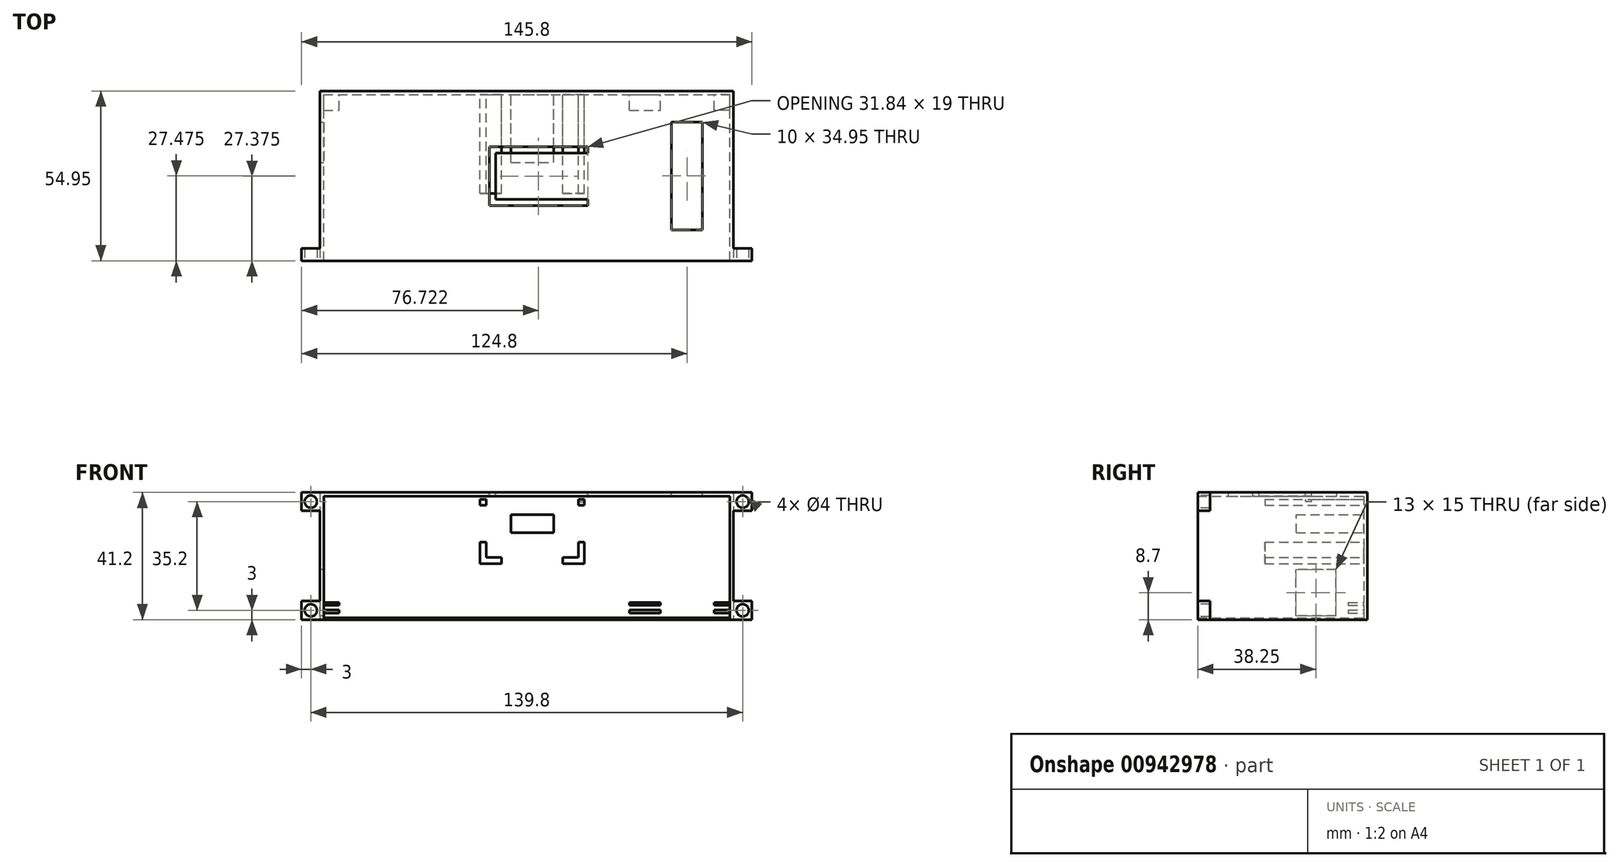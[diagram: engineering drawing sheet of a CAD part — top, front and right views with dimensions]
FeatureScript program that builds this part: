
annotation { "Feature Type Name" : "Feature", "Feature Type Description" : "" }
export const myFeature = defineFeature(function(context is Context, id is Id, definition is map)
    precondition{}
    {
        {
            var Q0;
            Q0=qCreatedBy(makeId("Top.planeOp"),FACE);
            var sketch = newSketch(context, id + "F0", { "sketchPlane" : qUnion([Q0])});
            skLineSegment(sketch, "E0.top", {"start": v(0, 53.75) * mm, "end": v(131.4, 53.75) * mm});
            skLineSegment(sketch, "E0.left", {"start": v(0, 0) * mm, "end": v(0, 53.75) * mm});
            skLineSegment(sketch, "E0.right", {"start": v(131.4, 0) * mm, "end": v(131.4, 53.75) * mm});
            skLineSegment(sketch, "E1.bottom", {"start": v(0, 0) * mm, "end": v(-1.2, 0) * mm});
            skLineSegment(sketch, "E1.top", {"start": v(0, 54.95) * mm, "end": v(-1.2, 54.95) * mm});
            skLineSegment(sketch, "E1.right", {"start": v(-1.2, 0) * mm, "end": v(-1.2, 54.95) * mm});
            skLineSegment(sketch, "E2.bottom", {"start": v(0, 54.95) * mm, "end": v(132.6, 54.95) * mm});
            skLineSegment(sketch, "E2.right", {"start": v(132.6, 54.95) * mm, "end": v(132.6, 53.75) * mm});
            skLineSegment(sketch, "E3.top", {"start": v(132.6, 0) * mm, "end": v(131.4, 0) * mm});
            skLineSegment(sketch, "E3.left", {"start": v(132.6, 53.75) * mm, "end": v(132.6, 0) * mm});
            skSolve(sketch);
        }
        {
            var Q0;
            Q0 = qSketchRegion(id + "F0", true);
            extrude(context, id + "F1", {"entities" : qUnion([Q0]), "depth" : 40 * mm, "offsetDistance" : 25 * mm});
        }
        {
            var Q0;
            Q0=makeQuery(id+"F1.opExtrude","CAP_FACE",FACE,{"disambiguationData":[OSD([sQuery(id+"F0.wireOp",EDGE,"E0.top"),sQuery(id+"F0.wireOp",EDGE,"E0.left"),sQuery(id+"F0.wireOp",EDGE,"E0.right"),sQuery(id+"F0.wireOp",EDGE,"E1.bottom"),sQuery(id+"F0.wireOp",EDGE,"E1.top"),sQuery(id+"F0.wireOp",EDGE,"E1.right"),sQuery(id+"F0.wireOp",EDGE,"E2.bottom"),sQuery(id+"F0.wireOp",EDGE,"E2.right"),sQuery(id+"F0.wireOp",EDGE,"E3.top"),sQuery(id+"F0.wireOp",EDGE,"E3.left")])],"isStart":true});
            var sketch = newSketch(context, id + "F2", { "sketchPlane" : qUnion([Q0])});
            skLineSegment(sketch, "E4.bottom", {"start": v(0, 0) * mm, "end": v(131.4, 0) * mm});
            skLineSegment(sketch, "E4.top", {"start": v(0, -53.75) * mm, "end": v(131.4, -53.75) * mm});
            skLineSegment(sketch, "E4.left", {"start": v(0, 0) * mm, "end": v(0, -53.75) * mm});
            skLineSegment(sketch, "E4.right", {"start": v(131.4, 0) * mm, "end": v(131.4, -53.75) * mm});
            skSolve(sketch);
        }
        {
            var Q0;
            Q0 = qSketchRegion(id + "F2", true);
            extrude(context, id + "F3", {"entities" : qUnion([Q0]), "oppositeDirection" : true, "depth" : 0.6 * mm, "offsetDistance" : 25 * mm});
        }
        {
            var Q0;
            Q0=makeQuery(id+"F1.opExtrude","SWEPT_FACE",FACE,{"disambiguationData":[OSD([sQuery(id+"F0.wireOp",EDGE,"E0.top")])]});
            var sketch = newSketch(context, id + "F4", { "sketchPlane" : qUnion([Q0])});
            skLineSegment(sketch, "E5.bottom", {"start": v(0, 2.1) * mm, "end": v(5, 2.1) * mm});
            skLineSegment(sketch, "E5.top", {"start": v(0, 3.1) * mm, "end": v(5, 3.1) * mm});
            skLineSegment(sketch, "E5.left", {"start": v(0, 2.1) * mm, "end": v(0, 3.1) * mm});
            skLineSegment(sketch, "E5.right", {"start": v(5, 2.1) * mm, "end": v(5, 3.1) * mm});
            skLineSegment(sketch, "E6.bottom", {"start": v(0, 4.6) * mm, "end": v(5, 4.6) * mm});
            skLineSegment(sketch, "E6.top", {"start": v(0, 5.6) * mm, "end": v(5, 5.6) * mm});
            skLineSegment(sketch, "E6.left", {"start": v(0, 4.6) * mm, "end": v(0, 5.6) * mm});
            skLineSegment(sketch, "E6.right", {"start": v(5, 4.6) * mm, "end": v(5, 5.6) * mm});
            skLineSegment(sketch, "E7.bottom", {"start": v(131.4, 2.1) * mm, "end": v(126.4, 2.1) * mm});
            skLineSegment(sketch, "E7.top", {"start": v(131.4, 3.1) * mm, "end": v(126.4, 3.1) * mm});
            skLineSegment(sketch, "E7.left", {"start": v(131.4, 2.1) * mm, "end": v(131.4, 3.1) * mm});
            skLineSegment(sketch, "E7.right", {"start": v(126.4, 2.1) * mm, "end": v(126.4, 3.1) * mm});
            skLineSegment(sketch, "E8.bottom", {"start": v(131.4, 4.6) * mm, "end": v(126.4, 4.6) * mm});
            skLineSegment(sketch, "E8.top", {"start": v(131.4, 5.6) * mm, "end": v(126.4, 5.6) * mm});
            skLineSegment(sketch, "E8.left", {"start": v(131.4, 4.6) * mm, "end": v(131.4, 5.6) * mm});
            skLineSegment(sketch, "E8.right", {"start": v(126.4, 4.6) * mm, "end": v(126.4, 5.6) * mm});
            skLineSegment(sketch, "E9.bottom", {"start": v(99, 3.1) * mm, "end": v(109, 3.1) * mm});
            skLineSegment(sketch, "E9.top", {"start": v(99, 2.1) * mm, "end": v(109, 2.1) * mm});
            skLineSegment(sketch, "E9.left", {"start": v(99, 3.1) * mm, "end": v(99, 2.1) * mm});
            skLineSegment(sketch, "E9.right", {"start": v(109, 3.1) * mm, "end": v(109, 2.1) * mm});
            skLineSegment(sketch, "E10.bottom", {"start": v(99, 4.6) * mm, "end": v(109, 4.6) * mm});
            skLineSegment(sketch, "E10.top", {"start": v(99, 5.6) * mm, "end": v(109, 5.6) * mm});
            skLineSegment(sketch, "E10.left", {"start": v(99, 4.6) * mm, "end": v(99, 5.6) * mm});
            skLineSegment(sketch, "E10.right", {"start": v(109, 4.6) * mm, "end": v(109, 5.6) * mm});
            skSolve(sketch);
        }
        {
            var Q0;
            Q0 = qSketchRegion(id + "F4", true);
            extrude(context, id + "F5", {"entities" : qUnion([Q0]), "operationType" : NewBodyOperationType.ADD, "depth" : 5 * mm, "offsetDistance" : 25 * mm});
        }
        {
            var Q0;
            Q0=makeQuery(id+"F1.opExtrude","SWEPT_FACE",FACE,{"disambiguationData":[OSD([sQuery(id+"F0.wireOp",EDGE,"E0.top")])]});
            var sketch = newSketch(context, id + "F6", { "sketchPlane" : qUnion([Q0])});
            skLineSegment(sketch, "E11.bottom", {"start": v(52.6, 39) * mm, "end": v(82.4, 39) * mm, "construction": true});
            skLineSegment(sketch, "E11.top", {"start": v(52.6, 20.1) * mm, "end": v(82.4, 20.1) * mm, "construction": true});
            skLineSegment(sketch, "E11.left", {"start": v(52.6, 39) * mm, "end": v(52.6, 20.1) * mm, "construction": true});
            skLineSegment(sketch, "E11.right", {"start": v(82.4, 39) * mm, "end": v(82.4, 20.1) * mm, "construction": true});
            skLineSegment(sketch, "E12", {"start": v(52.6, 20.1) * mm, "end": v(57.6, 20.1) * mm});
            skLineSegment(sketch, "E13", {"start": v(57.6, 20.1) * mm, "end": v(57.6, 18.1) * mm});
            skLineSegment(sketch, "E14", {"start": v(57.6, 18.1) * mm, "end": v(50.6, 18.1) * mm});
            skLineSegment(sketch, "E15", {"start": v(50.6, 18.1) * mm, "end": v(50.6, 25.1) * mm});
            skLineSegment(sketch, "E16", {"start": v(50.6, 25.1) * mm, "end": v(52.6, 25.1) * mm});
            skLineSegment(sketch, "E17", {"start": v(52.6, 25.1) * mm, "end": v(52.6, 20.1) * mm});
            skLineSegment(sketch, "E18", {"start": v(77.4, 20.1) * mm, "end": v(82.4, 20.1) * mm});
            skLineSegment(sketch, "E19", {"start": v(82.4, 25.1) * mm, "end": v(84.4, 25.1) * mm});
            skLineSegment(sketch, "E20", {"start": v(84.4, 25.1) * mm, "end": v(84.4, 18.1) * mm});
            skLineSegment(sketch, "E21", {"start": v(84.4, 18.1) * mm, "end": v(77.4, 18.1) * mm});
            skLineSegment(sketch, "E22", {"start": v(77.4, 18.1) * mm, "end": v(77.4, 20.1) * mm});
            skLineSegment(sketch, "E23.bottom", {"start": v(82.4, 39) * mm, "end": v(84.4, 39) * mm});
            skLineSegment(sketch, "E23.top", {"start": v(82.4, 37) * mm, "end": v(84.4, 37) * mm});
            skLineSegment(sketch, "E23.left", {"start": v(82.4, 39) * mm, "end": v(82.4, 37) * mm});
            skLineSegment(sketch, "E23.right", {"start": v(84.4, 39) * mm, "end": v(84.4, 37) * mm});
            skLineSegment(sketch, "E24.bottom", {"start": v(52.6, 39) * mm, "end": v(50.6, 39) * mm});
            skLineSegment(sketch, "E24.top", {"start": v(52.6, 37) * mm, "end": v(50.6, 37) * mm});
            skLineSegment(sketch, "E24.left", {"start": v(52.6, 39) * mm, "end": v(52.6, 37) * mm});
            skLineSegment(sketch, "E24.right", {"start": v(50.6, 39) * mm, "end": v(50.6, 37) * mm});
            skLineSegment(sketch, "E25", {"start": v(82.4, 20.1) * mm, "end": v(82.4, 25.1) * mm});
            skSolve(sketch);
        }
        {
            var Q0;
            Q0 = qSketchRegion(id + "F6", true);
            var Q1;
            Q1=makeQuery(id+"F1.opExtrude","SWEPT_BODY",BODY,{"disambiguationData":[OSD([sQuery(id+"F0.wireOp",EDGE,"E0.top"),sQuery(id+"F0.wireOp",EDGE,"E0.left"),sQuery(id+"F0.wireOp",EDGE,"E0.right"),sQuery(id+"F0.wireOp",EDGE,"E1.bottom"),sQuery(id+"F0.wireOp",EDGE,"E1.top"),sQuery(id+"F0.wireOp",EDGE,"E1.right"),sQuery(id+"F0.wireOp",EDGE,"E2.bottom"),sQuery(id+"F0.wireOp",EDGE,"E2.right"),sQuery(id+"F0.wireOp",EDGE,"E3.top"),sQuery(id+"F0.wireOp",EDGE,"E3.left")])]});
            extrude(context, id + "F7", {"entities" : qUnion([Q0]), "operationType" : NewBodyOperationType.ADD, "depth" : 32 * mm, "endBoundEntityBody" : qUnion([Q1]), "offsetDistance" : 25 * mm});
        }
        {
            var Q0;
            Q0=makeQuery(id+"F1.opExtrude","SWEPT_FACE",FACE,{"disambiguationData":[OSD([sQuery(id+"F0.wireOp",EDGE,"E0.top")])]});
            var sketch = newSketch(context, id + "F8", { "sketchPlane" : qUnion([Q0])});
            skLineSegment(sketch, "E26.bottom", {"start": v(60.6, 28.1) * mm, "end": v(74.4, 28.1) * mm});
            skLineSegment(sketch, "E26.top", {"start": v(60.6, 34) * mm, "end": v(74.4, 34) * mm});
            skLineSegment(sketch, "E26.left", {"start": v(60.6, 28.1) * mm, "end": v(60.6, 34) * mm});
            skLineSegment(sketch, "E26.right", {"start": v(74.4, 28.1) * mm, "end": v(74.4, 34) * mm});
            skSolve(sketch);
        }
        {
            var Q0;
            Q0 = qSketchRegion(id + "F8", true);
            extrude(context, id + "F9", {"entities" : qUnion([Q0]), "operationType" : NewBodyOperationType.ADD, "depth" : (53.75 / 2 - 5) * mm, "offsetDistance" : 25 * mm});
        }
        {
            var Q0;
            Q0=makeQuery(id+"F1.opExtrude","SWEPT_FACE",FACE,{"disambiguationData":[OSD([sQuery(id+"F0.wireOp",EDGE,"E1.top"),sQuery(id+"F0.wireOp",EDGE,"E2.bottom")])]});
            var sketch = newSketch(context, id + "F10", { "sketchPlane" : qUnion([Q0])});
            skLineSegment(sketch, "E27.bottom", {"start": v(-131.4, 40) * mm, "end": v(-132.6, 40) * mm});
            skLineSegment(sketch, "E27.top", {"start": v(-127.4, 41.2) * mm, "end": v(-132.6, 41.2) * mm});
            skLineSegment(sketch, "E27.right", {"start": v(-132.6, 40) * mm, "end": v(-132.6, 41.2) * mm});
            skLineSegment(sketch, "E28.bottom", {"start": v(1.2, 40) * mm, "end": v(-127.4, 40) * mm});
            skLineSegment(sketch, "E28.top", {"start": v(1.2, 41.2) * mm, "end": v(-127.4, 41.2) * mm});
            skLineSegment(sketch, "E28.left", {"start": v(1.2, 40) * mm, "end": v(1.2, 41.2) * mm});
            skLineSegment(sketch, "E29", {"start": v(-127.4, 40) * mm, "end": v(-131.4, 40) * mm});
            skSolve(sketch);
        }
        {
            var Q0;
            Q0 = qSketchRegion(id + "F10", true);
            var Q1;
            Q1=makeQuery(id+"F1.opExtrude","SWEPT_FACE",FACE,{"disambiguationData":[OSD([sQuery(id+"F0.wireOp",EDGE,"E1.bottom")])]});
            extrude(context, id + "F11", {"entities" : qUnion([Q0]), "operationType" : NewBodyOperationType.ADD, "endBound" : BoundingType.UP_TO_SURFACE, "oppositeDirection" : true, "depth" : 25 * mm, "endBoundEntityFace" : qUnion([Q1]), "offsetDistance" : 25 * mm});
        }
        {
            var Q0;
            Q0=makeQuery(id+"F11.opExtrude","SWEPT_FACE",FACE,{"disambiguationData":[OSD([sQuery(id+"F10.wireOp",EDGE,"E27.top"),sQuery(id+"F10.wireOp",EDGE,"E28.top")])]});
            var sketch = newSketch(context, id + "F12", { "sketchPlane" : qUnion([Q0])});
            skLineSegment(sketch, "E30", {"start": v(85.44, 36.88) * mm, "end": v(53.6, 36.88) * mm});
            skLineSegment(sketch, "E31", {"start": v(53.6, 36.88) * mm, "end": v(53.6, 17.88) * mm});
            skLineSegment(sketch, "E32", {"start": v(53.6, 17.88) * mm, "end": v(85.44, 17.88) * mm});
            skLineSegment(sketch, "E33", {"start": v(85.44, 17.88) * mm, "end": v(85.44, 19.88) * mm});
            skLineSegment(sketch, "E34", {"start": v(85.44, 19.88) * mm, "end": v(55.6, 19.88) * mm});
            skLineSegment(sketch, "E35", {"start": v(55.6, 19.87) * mm, "end": v(55.6, 34.87) * mm});
            skLineSegment(sketch, "E36", {"start": v(55.6, 34.87) * mm, "end": v(85.44, 34.87) * mm});
            skLineSegment(sketch, "E37", {"start": v(85.44, 34.87) * mm, "end": v(85.44, 36.88) * mm});
            skLineSegment(sketch, "E38.bottom", {"start": v(122.6, 10) * mm, "end": v(112.6, 10) * mm});
            skLineSegment(sketch, "E38.top", {"start": v(122.6, 44.95) * mm, "end": v(112.6, 44.95) * mm});
            skLineSegment(sketch, "E38.left", {"start": v(122.6, 10) * mm, "end": v(122.6, 44.95) * mm});
            skLineSegment(sketch, "E38.right", {"start": v(112.6, 10) * mm, "end": v(112.6, 44.95) * mm});
            skSolve(sketch);
        }
        {
            var Q0;
            Q0 = qSketchRegion(id + "F12", true);
            extrude(context, id + "F13", {"entities" : qUnion([Q0]), "operationType" : NewBodyOperationType.REMOVE, "oppositeDirection" : true, "depth" : 3 * mm, "offsetDistance" : 25 * mm});
        }
        {
            var Q0;
            Q0=makeQuery(id+"F11.boolean.opBoolean","MERGE",FACE,{"derivedFrom":[makeQuery(id+"F1.opExtrude","SWEPT_FACE",FACE,{"disambiguationData":[OSD([sQuery(id+"F0.wireOp",EDGE,"E1.right")])]}),makeQuery(id+"F11.opExtrude","SWEPT_FACE",FACE,{"disambiguationData":[OSD([sQuery(id+"F10.wireOp",EDGE,"E28.left")])]})]});
            var sketch = newSketch(context, id + "F14", { "sketchPlane" : qUnion([Q0])});
            skLineSegment(sketch, "E39.bottom", {"start": v(-44.75, 1.2) * mm, "end": v(-31.75, 1.2) * mm});
            skLineSegment(sketch, "E39.top", {"start": v(-44.75, 16.2) * mm, "end": v(-31.75, 16.2) * mm});
            skLineSegment(sketch, "E39.left", {"start": v(-44.75, 1.2) * mm, "end": v(-44.75, 16.2) * mm});
            skLineSegment(sketch, "E39.right", {"start": v(-31.75, 1.2) * mm, "end": v(-31.75, 16.2) * mm});
            skSolve(sketch);
        }
        {
            var Q0;
            Q0 = qSketchRegion(id + "F14", true);
            extrude(context, id + "F15", {"entities" : qUnion([Q0]), "operationType" : NewBodyOperationType.REMOVE, "oppositeDirection" : true, "depth" : 25 * mm, "offsetDistance" : 25 * mm});
        }
        {
            var Q0;
            Q0=makeQuery(id+"F11.boolean.opBoolean","MERGE",FACE,{"derivedFrom":[makeQuery(id+"F1.opExtrude","SWEPT_FACE",FACE,{"disambiguationData":[OSD([sQuery(id+"F0.wireOp",EDGE,"E1.bottom")])]}),makeQuery(id+"F1.opExtrude","SWEPT_FACE",FACE,{"disambiguationData":[OSD([sQuery(id+"F0.wireOp",EDGE,"E3.top")])]}),makeQuery(id+"F11.opExtrude","CAP_FACE",FACE,{"disambiguationData":[OSD([sQuery(id+"F10.wireOp",EDGE,"E27.bottom"),sQuery(id+"F10.wireOp",EDGE,"E27.top"),sQuery(id+"F10.wireOp",EDGE,"E27.right"),sQuery(id+"F10.wireOp",EDGE,"E28.bottom"),sQuery(id+"F10.wireOp",EDGE,"E28.top"),sQuery(id+"F10.wireOp",EDGE,"E28.left"),sQuery(id+"F10.wireOp",EDGE,"E29")])],"isStart":false})]});
            var sketch = newSketch(context, id + "F16", { "sketchPlane" : qUnion([Q0])});
            skLineSegment(sketch, "E40.bottom", {"start": v(-1.2, 0) * mm, "end": v(-7.2, 0) * mm});
            skLineSegment(sketch, "E40.top", {"start": v(-1.2, 6) * mm, "end": v(-7.2, 6) * mm});
            skLineSegment(sketch, "E40.left", {"start": v(-1.2, 0) * mm, "end": v(-1.2, 6) * mm});
            skLineSegment(sketch, "E40.right", {"start": v(-7.2, 0) * mm, "end": v(-7.2, 6) * mm});
            skCircle(sketch, "E41", {"center": v(-4.2, 3) * mm, "radius": 2 * mm});
            skPoint(sketch, "E41.centerSnap0", {"position": v(-4.2, 0) * mm});
            skPoint(sketch, "E41.centerSnap1", {"position": v(-7.2, 3) * mm});
            skLineSegment(sketch, "E42.bottom", {"start": v(-1.2, 41.2) * mm, "end": v(-7.2, 41.2) * mm});
            skLineSegment(sketch, "E42.top", {"start": v(-1.2, 35.2) * mm, "end": v(-7.2, 35.2) * mm});
            skLineSegment(sketch, "E42.left", {"start": v(-1.2, 41.2) * mm, "end": v(-1.2, 35.2) * mm});
            skLineSegment(sketch, "E42.right", {"start": v(-7.2, 41.2) * mm, "end": v(-7.2, 35.2) * mm});
            skLineSegment(sketch, "E43.bottom", {"start": v(132.6, 41.2) * mm, "end": v(138.6, 41.2) * mm});
            skLineSegment(sketch, "E43.top", {"start": v(132.6, 35.2) * mm, "end": v(138.6, 35.2) * mm});
            skLineSegment(sketch, "E43.left", {"start": v(132.6, 41.2) * mm, "end": v(132.6, 35.2) * mm});
            skLineSegment(sketch, "E43.right", {"start": v(138.6, 41.2) * mm, "end": v(138.6, 35.2) * mm});
            skLineSegment(sketch, "E44.bottom", {"start": v(132.6, 0) * mm, "end": v(138.6, 0) * mm});
            skLineSegment(sketch, "E44.top", {"start": v(132.6, 6) * mm, "end": v(138.6, 6) * mm});
            skLineSegment(sketch, "E44.left", {"start": v(132.6, 0) * mm, "end": v(132.6, 6) * mm});
            skLineSegment(sketch, "E44.right", {"start": v(138.6, 0) * mm, "end": v(138.6, 6) * mm});
            skCircle(sketch, "E45", {"center": v(135.6, 3) * mm, "radius": 2 * mm});
            skPoint(sketch, "E45.centerSnap0", {"position": v(132.6, 3) * mm});
            skPoint(sketch, "E45.centerSnap1", {"position": v(135.6, 0) * mm});
            skPoint(sketch, "E45.perimeterSnap0", {"position": v(132.6, 3) * mm});
            skCircle(sketch, "E46", {"center": v(135.6, 38.2) * mm, "radius": 2 * mm});
            skPoint(sketch, "E46.centerSnap0", {"position": v(132.6, 38.2) * mm});
            skPoint(sketch, "E46.centerSnap1", {"position": v(135.6, 41.2) * mm});
            skCircle(sketch, "E47", {"center": v(-4.2, 38.2) * mm, "radius": 2 * mm});
            skPoint(sketch, "E47.centerSnap0", {"position": v(-4.2, 41.2) * mm});
            skPoint(sketch, "E47.centerSnap1", {"position": v(-1.2, 38.2) * mm});
            skSolve(sketch);
        }
        {
            var Q0;
            Q0 = qSketchRegion(id + "F16", true);
            extrude(context, id + "F17", {"entities" : qUnion([Q0]), "operationType" : NewBodyOperationType.ADD, "oppositeDirection" : true, "depth" : 4 * mm, "offsetDistance" : 25 * mm});
        }
    });
